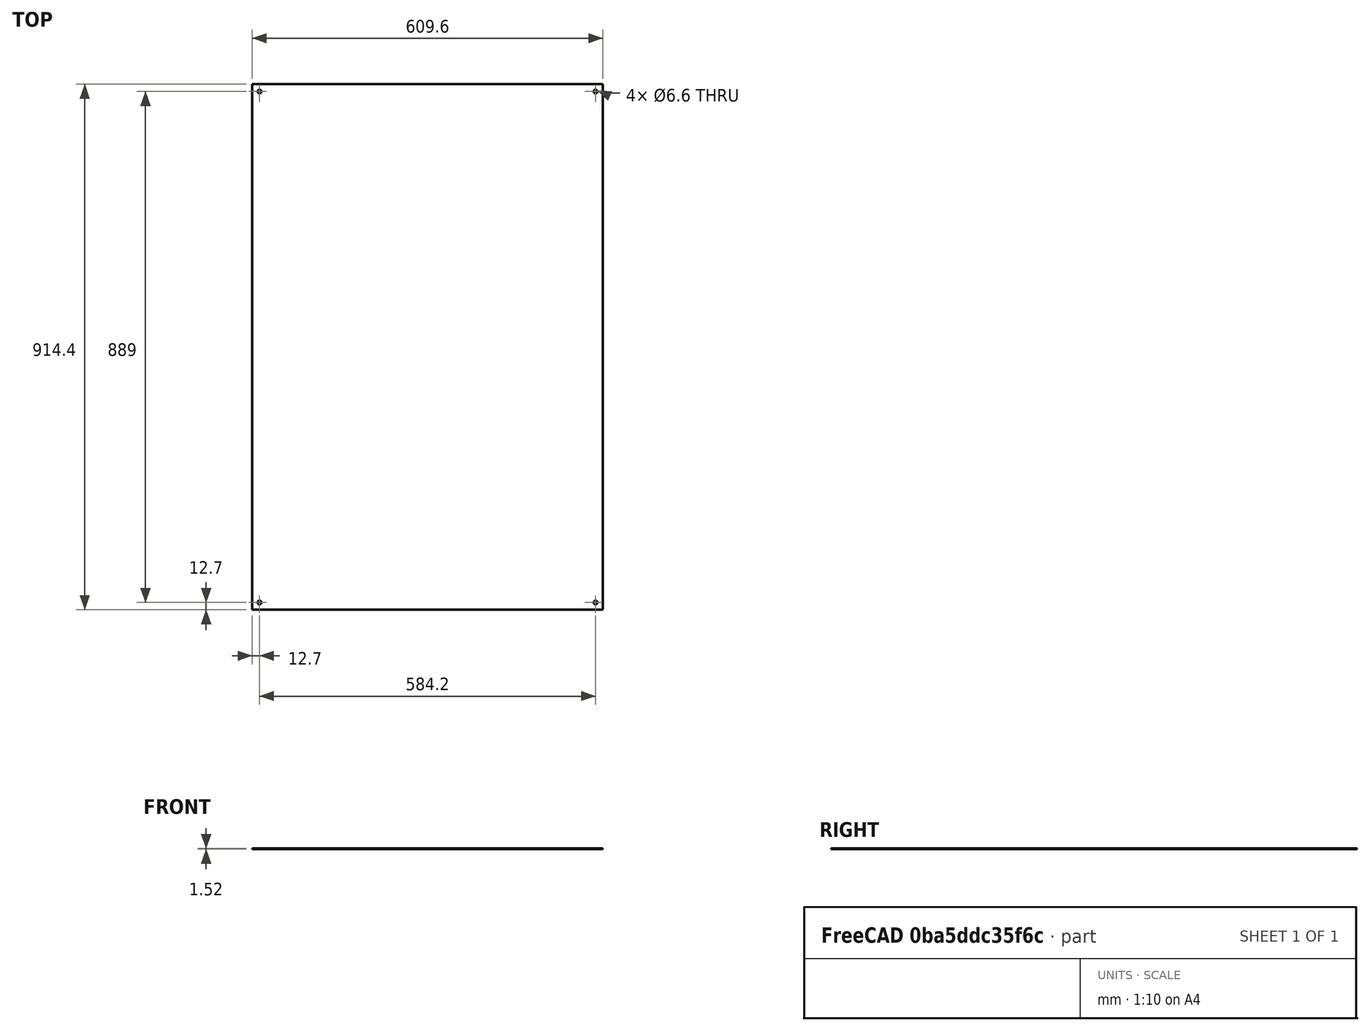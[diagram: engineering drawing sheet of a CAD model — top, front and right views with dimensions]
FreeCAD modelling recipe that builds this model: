
FCSTD DOCUMENT  (FreeCAD 0.21R33694 (Git))
Label: Steel_Sheet_24inx36inx16ga
License: All rights reserved
LicenseURL: http://en.wikipedia.org/wiki/All_rights_reserved
objects: Sketcher::SketchObject×1, PartDesign::Pad×1, PartDesign::Body×1
note: 4 computed .brp shape members not serialized (recipe doc carries the construction recipe); baked Part::Feature solids carry a one-line shape summary decoded from their .brp

FEATURE [Sketcher::SketchObject] Sketch
  FullyConstrained = true
  MapMode = 5
  Support = -> [XY_Plane]
  sketch-geometry (16):
    g0: LineSegment StartX=-304.8 StartY=457.2 StartZ=0 EndX=304.8 EndY=457.2 EndZ=0
    g1: LineSegment StartX=304.8 StartY=457.2 StartZ=0 EndX=304.8 EndY=-457.2 EndZ=0
    g2: LineSegment StartX=304.8 StartY=-457.2 StartZ=0 EndX=-304.8 EndY=-457.2 EndZ=0
    g3: LineSegment StartX=-304.8 StartY=-457.2 StartZ=0 EndX=-304.8 EndY=457.2 EndZ=0
    g4: LineSegment StartX=304.8 StartY=457.2 StartZ=0 EndX=292.1 EndY=457.2 EndZ=0
    g5: LineSegment StartX=292.1 StartY=457.2 StartZ=0 EndX=292.1 EndY=444.5 EndZ=0
    g6: Circle CenterX=292.1 CenterY=444.5 CenterZ=0 NormalX=0 NormalY=0 NormalZ=1 AngleXU=0 Radius=3.3
    g7: LineSegment StartX=-304.8 StartY=457.2 StartZ=0 EndX=-292.1 EndY=457.2 EndZ=0
    g8: LineSegment StartX=-292.1 StartY=457.2 StartZ=0 EndX=-292.1 EndY=444.5 EndZ=0
    g9: Circle CenterX=-292.1 CenterY=444.5 CenterZ=0 NormalX=0 NormalY=0 NormalZ=1 AngleXU=0 Radius=3.3
    g10: LineSegment StartX=-304.8 StartY=-457.2 StartZ=0 EndX=-292.1 EndY=-457.2 EndZ=0
    g11: LineSegment StartX=-292.1 StartY=-457.2 StartZ=0 EndX=-292.1 EndY=-444.5 EndZ=0
    g12: Circle CenterX=-292.1 CenterY=-444.5 CenterZ=0 NormalX=0 NormalY=0 NormalZ=1 AngleXU=0 Radius=3.3
    g13: LineSegment StartX=304.8 StartY=-457.2 StartZ=0 EndX=292.1 EndY=-457.2 EndZ=0
    g14: LineSegment StartX=292.1 StartY=-457.2 StartZ=0 EndX=292.1 EndY=-444.5 EndZ=0
    g15: Circle CenterX=292.1 CenterY=-444.5 CenterZ=0 NormalX=0 NormalY=0 NormalZ=1 AngleXU=0 Radius=3.3
  constraints (43):
    c: Coincident(g0,g1)
    c: Coincident(g1,g2)
    c: Coincident(g2,g3)
    c: Coincident(g3,g0)
    c: Horizontal(g0)
    c: Horizontal(g2)
    c: Vertical(g1)
    c: Vertical(g3)
    c: Symmetric(g2,g0,g-1)
    c: DistanceX(g0,g0) = 609.6
    c: Coincident(g4,g5)
    c: Horizontal(g4)
    c: Vertical(g5)
    c: Coincident(g4,g0)
    c: DistanceX(g4,g4) = 12.7
    c: Coincident(g6,g5)
    c: Coincident(g7,g8)
    c: Horizontal(g7)
    c: Vertical(g8)
    c: Coincident(g7,g0)
    c: Coincident(g9,g8)
    c: Coincident(g10,g11)
    c: Horizontal(g10)
    c: Vertical(g11)
    c: Coincident(g10,g2)
    c: Coincident(g12,g11)
    c: Coincident(g13,g14)
    c: Horizontal(g13)
    c: Vertical(g14)
    c: Coincident(g13,g1)
    c: Coincident(g15,g14)
    c: DistanceY(g1,g1) = 914.4
    c: Horizontal(g9,g6)
    c: Horizontal(g12,g15)
    c: Vertical(g6,g15)
    c: Vertical(g12,g9)
    c: DistanceX(g7,g7) = 12.7
    c: DistanceY(g8,g8) = 12.7
    c: Diameter(g9) = 6.6
    c: Equal(g6,g9)
    c: Equal(g9,g12)
    c: Equal(g12,g15)
    c: DistanceY(g11,g11) = 12.7
FEATURE [PartDesign::Pad] Pad
  Direction = (0,0,1)
  Length = 1.519
  Length2 = 10
  Profile = -> Sketch
  ReferenceAxis = -> Sketch [N_Axis]
  Type = 0
FEATURE [PartDesign::Body] Body
  Group = -> [Sketch,Pad]
  Origin = -> Origin
  Tip = -> Pad
